# Revit family: HCL_Latchways_FallArrstSymGddAnchrLine_LadderLatch_SquareRungStandard
name_source: partatom
category: Specialty Equipment
revit_build: Autodesk Revit 2014 (Build: 20130308_1515(x64)
units: mm (PartAtom-declared; Revit-internal decimal feet)

## types (3) — shared parameters
AssetType = Fixed
BottomAnchorMaterial = LWplc_Latchways_StainlessSteel_MarineGrade316
Default Elevation = 1219 mm
DurationUnit = year
EnergyAbsorberMaterial = LWplc_Latchways_PVCu_Vinakon_Black
FireExit = No
IfcExportAs = NOTDEFINED
IfcExportType = IfcTransportElement
Installer Website = https://www.hclsafety.com
ManufacturerName = MSA Latchways
ManufacturerURL = www.latchways.com
Material = All critical components are manufactured from stainless steel grade 316
ModelReference = LadderLatch Vertical Fall Arrest Systems
NBSDescription = Fall arrest system - guided anchor line
NBSReference = 80-50-25/110
ProductInformation = https://www.hclsafety.com
RodMaterial = LWplc_Latchways_StainlessSteel_MarineGrade316
TopAnchorMaterial = LWplc_Latchways_StainlessSteel_MarineGrade316
URL = www.latchways.com
Uniclass2 = Ss_80_30_25_35
Version = 1
WarrantyDurationUnit = year
WireGuideMaterial = LWplc_Latchways_StainlessSteel_MarineGrade316
zero-valued in all types: NominalHeight, NominalLength, NominalWidth

## per-type parameters (varying)
| type | BIMObjectName | BottomAnchorVisible | Description | EnergyAbsorberVisible | TopAnchorVisible | WireGuideVisible |
| FallArrestSystemGuidedAnchorLine_LadderLatch_SquareRungStandardBottomAnchor_MSA_Latchways | HCL_Latchways_FallArrestSystemGuidedAnchorLine_LadderLatch_SquareRungStandardBottomAnchor | Yes | Latchways' LadderLatch systems combine revolutionary Constant
Force® technology with an innovative mobile anchorage device. With the capacity for multiple workers to be attached, the system offers unhindered mobility and continuous, hands-free security to ensure 3 points of contact whilst ascending and descending ladders. System compliant with latest EN 353-1:2014 standard | No | No | No |
| FallArrestSystemGuidedAnchorLine_LadderLatch_SquareRungStandardTopAnchor_MSA_Latchways | HCL_Latchways_FallArrestSystemGuidedAnchorLine_LadderLatch_SquareRungStandardTopAnchor | No | Latchways' LadderLatch systems combine revolutionary Constant
Force® technology with an innovative mobile anchorage device. With the capacity for multiple workers to be attached, the system offers unhindered mobility and continuous, hands-free security to ensure 3 points of contact whilst ascending and descending ladders. System compliant with latest EN 353-1:2014 standard | Yes | Yes | No |
| FallArrestSystemGuidedAnchorLine_LadderLatch_SquareRungStandardWireGuide_MSA_Latchways | HCL_Latchways_FallArrestSystemGuidedAnchorLine_LadderLatch_SquareRungStandardWireGuide | No | Latchways' LadderLatch systems combine revolutionary Constant
Force® technology with an innovative mobile anchorage device. With the capacity for multiple workers to be attached, the system offers unhindered mobility and continuous, hands-free security to ensure 3 points of contact whilst ascending and descending ladders. System compliant with latest EN 353-1:2014 standard
Force® technology with an innovative mobile anchorage device. With the capacity for multiple workers to be attached, the system offers unhindered mobilty and continuous, hands-free security to ensure 3 points of contact whilst assending and desending ladders. System compliant with latest EN 353-1:2014 standard | No | No | Yes |

note: column(s) folded — value = type name in every type: Name

## geometry (parser evidence)
native form markers: Sweep x17
no freeform markers — native parametric forms only
